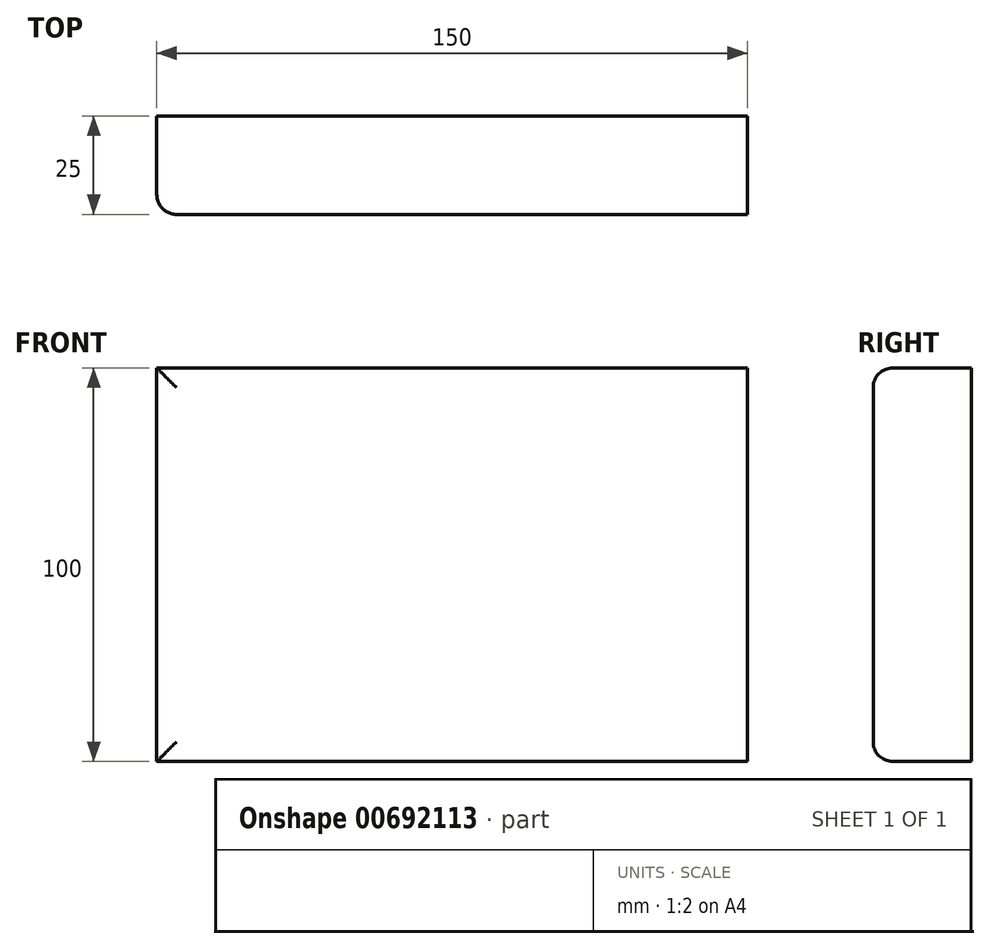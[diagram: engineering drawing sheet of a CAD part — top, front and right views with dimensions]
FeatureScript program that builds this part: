
annotation { "Feature Type Name" : "Feature", "Feature Type Description" : "" }
export const myFeature = defineFeature(function(context is Context, id is Id, definition is map)
    precondition{}
    {
        {
            var Q0;
            Q0=qCreatedBy(makeId("Front.planeOp"),FACE);
            var sketch = newSketch(context, id + "F0", { "sketchPlane" : qUnion([Q0])});
            skLineSegment(sketch, "E0.bottom", {"start": v(83.2, -50) * mm, "end": v(-66.8, -50) * mm});
            skLineSegment(sketch, "E0.top", {"start": v(83.2, 50) * mm, "end": v(-66.8, 50) * mm});
            skLineSegment(sketch, "E0.right", {"start": v(-66.8, -50) * mm, "end": v(-66.8, 50) * mm});
            skLineSegment(sketch, "E1.0", {"start": v(89.32, -30.05) * mm, "end": v(88.62, -29.58) * mm});
            skLineSegment(sketch, "E2.0", {"start": v(98.34, -18.03) * mm, "end": v(96.94, -17.1) * mm});
            skLineSegment(sketch, "E3", {"start": v(83.2, -50) * mm, "end": v(83.2, 50) * mm});
            skSolve(sketch);
        }
        {
            var Q0;
            Q0 = qSketchRegion(id + "F0", true);
            extrude(context, id + "F1", {"entities" : qUnion([Q0]), "depth" : 25 * mm, "offsetDistance" : 25 * mm});
        }
        {
            var Q0;
            Q0=makeQuery(id+"F1.opExtrude","CAP_EDGE",EDGE,{"disambiguationData":[OSD([sQuery(id+"F0.wireOp",EDGE,"E0.top")])],"isStart":false});
            var Q1;
            Q1=makeQuery(id+"F1.opExtrude","CAP_EDGE",EDGE,{"disambiguationData":[OSD([sQuery(id+"F0.wireOp",EDGE,"E0.right")])],"isStart":false});
            var Q2;
            Q2=makeQuery(id+"F1.opExtrude","CAP_EDGE",EDGE,{"disambiguationData":[OSD([sQuery(id+"F0.wireOp",EDGE,"E0.bottom")])],"isStart":false});
            var Q3;
            Q3=makeQuery(id+"F1.opExtrude","CAP_EDGE",EDGE,{"disambiguationData":[OSD([sQuery(id+"F0.wireOp",EDGE,"E0.left")])],"isStart":false});
            fillet(context, id + "F2", {"entities" : qUnion([Q0, Q1, Q2, Q3]), "radius" : 5 * mm, "tangentPropagation" : true, "allowEdgeOverflow" : false});
        }
    });
